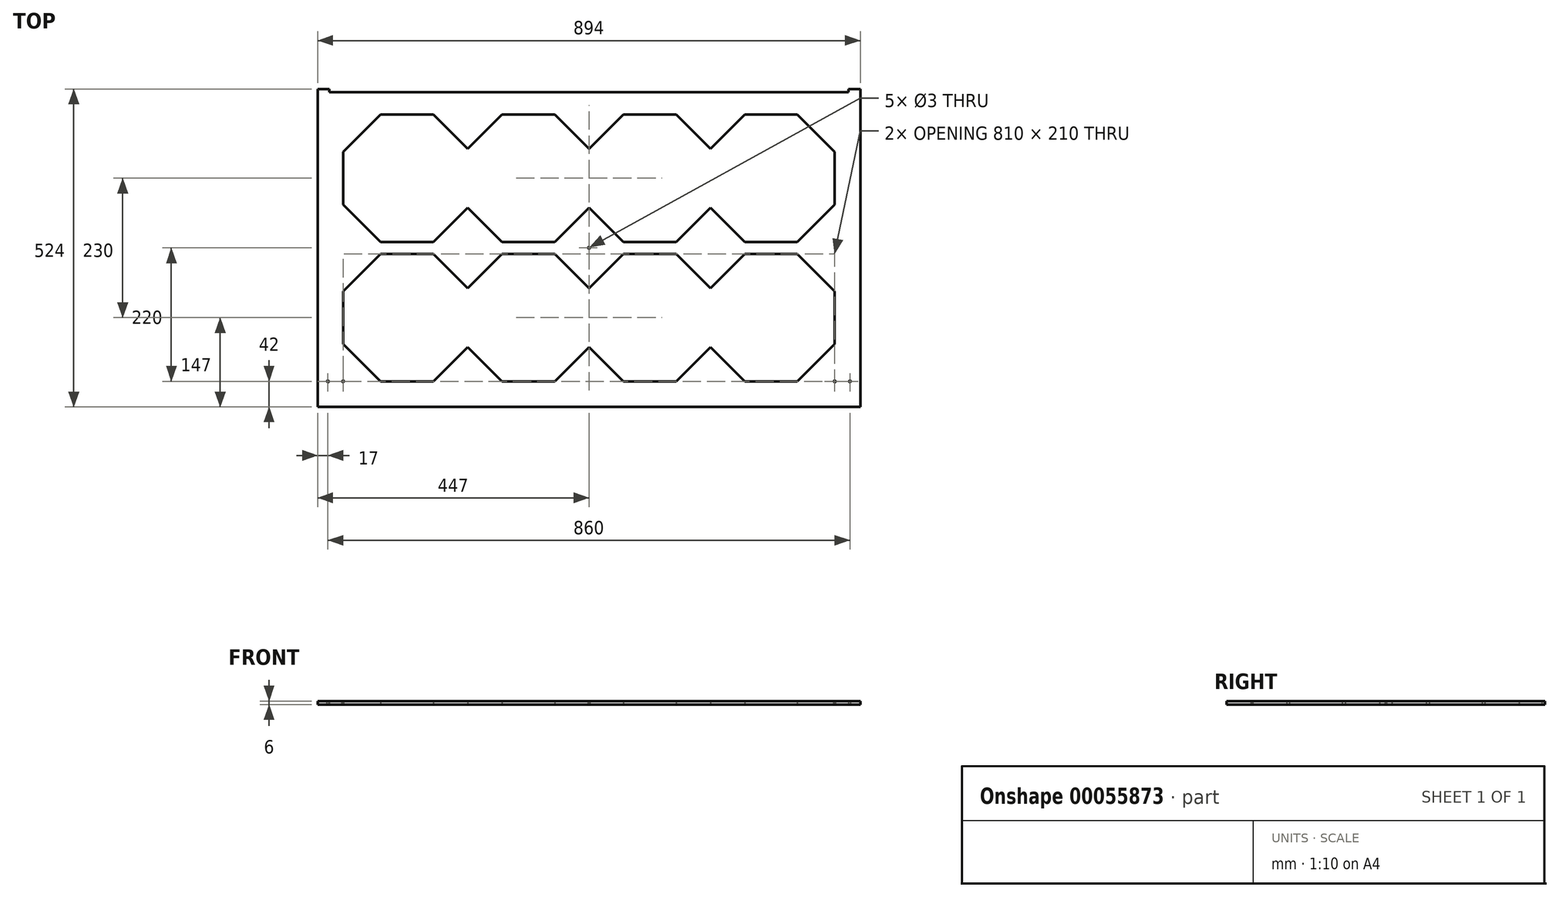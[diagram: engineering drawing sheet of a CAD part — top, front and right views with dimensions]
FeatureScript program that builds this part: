
annotation { "Feature Type Name" : "Feature", "Feature Type Description" : "" }
export const myFeature = defineFeature(function(context is Context, id is Id, definition is map)
    precondition{}
    {
        {
            var Q0;
            Q0=qCreatedBy(makeId("Top.planeOp"),FACE);
            var sketch = newSketch(context, id + "F0", { "sketchPlane" : qUnion([Q0])});
            skCircle(sketch, "E0.cCircle", {"center": v(0, 0) * mm, "radius": 100 * mm, "construction": true});
            skLineSegment(sketch, "E0.0", {"start": v(-41.42, 100) * mm, "end": v(41.42, 100) * mm});
            skLineSegment(sketch, "E0.1", {"start": v(41.42, 100) * mm, "end": v(100, 41.42) * mm});
            skLineSegment(sketch, "E0.2", {"start": v(100, 41.42) * mm, "end": v(100, -41.42) * mm});
            skLineSegment(sketch, "E0.3", {"start": v(100, -41.42) * mm, "end": v(41.42, -100) * mm});
            skLineSegment(sketch, "E0.4", {"start": v(41.42, -100) * mm, "end": v(-41.42, -100) * mm});
            skLineSegment(sketch, "E0.5", {"start": v(-41.42, -100) * mm, "end": v(-100, -41.42) * mm});
            skLineSegment(sketch, "E0.6", {"start": v(-100, -41.42) * mm, "end": v(-100, 41.42) * mm});
            skLineSegment(sketch, "E0.7", {"start": v(-100, 41.42) * mm, "end": v(-41.42, 100) * mm});
            skPoint(sketch, "E0.0.midPoint", {"position": v(0, 100) * mm});
            skCircle(sketch, "E1", {"center": v(-31.79, 31.79) * mm, "radius": 1.3 * mm, "construction": true});
            skCircle(sketch, "E2", {"center": v(31.79, 31.79) * mm, "radius": 1.3 * mm, "construction": true});
            skCircle(sketch, "E3", {"center": v(-31.79, -31.79) * mm, "radius": 1.3 * mm, "construction": true});
            skCircle(sketch, "E4", {"center": v(31.79, -31.79) * mm, "radius": 1.3 * mm, "construction": true});
            skLineSegment(sketch, "E5", {"start": v(0, 0) * mm, "end": v(13.6, 0) * mm, "construction": true});
            skPoint(sketch, "E6", {"position": v(0, -42.85) * mm});
            skLineSegment(sketch, "E7", {"start": v(0, -42.85) * mm, "end": v(66.68, -42.85) * mm, "construction": true});
            skLineSegment(sketch, "E8", {"start": v(0, -42.85) * mm, "end": v(-66.68, -42.85) * mm, "construction": true});
            skCircle(sketch, "E9", {"center": v(-66.68, -42.85) * mm, "radius": 3.81 * mm});
            skCircle(sketch, "E10", {"center": v(66.68, -42.85) * mm, "radius": 3.81 * mm});
            skLineSegment(sketch, "E11", {"start": v(0, 0) * mm, "end": v(0, -42.85) * mm, "construction": true});
            skLineSegment(sketch, "E12.bottom", {"start": v(765, -453) * mm, "end": v(-147, -453) * mm, "construction": true});
            skLineSegment(sketch, "E12.top", {"start": v(765, 147) * mm, "end": v(705, 147) * mm, "construction": true});
            skLineSegment(sketch, "E12.left", {"start": v(765, -453) * mm, "end": v(765, 147) * mm, "construction": true});
            skLineSegment(sketch, "E12.right", {"start": v(-147, -453) * mm, "end": v(-147, 147) * mm, "construction": true});
            skPoint(sketch, "E12.middle", {"position": v(309, -153) * mm});
            skLineSegment(sketch, "E13.0", {"start": v(-43.5, 105) * mm, "end": v(43.5, 105) * mm});
            skLineSegment(sketch, "E13.1", {"start": v(-105, 43.5) * mm, "end": v(-43.5, 105) * mm});
            skLineSegment(sketch, "E13.2", {"start": v(43.5, 105) * mm, "end": v(105, 43.5) * mm});
            skLineSegment(sketch, "E13.3", {"start": v(-105, -43.5) * mm, "end": v(-105, 43.5) * mm});
            skLineSegment(sketch, "E13.4", {"start": v(105, 43.5) * mm, "end": v(105, -43.5) * mm});
            skLineSegment(sketch, "E13.5", {"start": v(105, -43.5) * mm, "end": v(43.5, -105) * mm});
            skLineSegment(sketch, "E13.6", {"start": v(43.5, -105) * mm, "end": v(-43.5, -105) * mm});
            skLineSegment(sketch, "E13.7", {"start": v(-43.5, -105) * mm, "end": v(-105, -43.5) * mm});
            skLineSegment(sketch, "E14.0.1.0", {"start": v(0, -272.85) * mm, "end": v(66.68, -272.85) * mm, "construction": true});
            skLineSegment(sketch, "E14.0.1.1", {"start": v(-43.5, -335) * mm, "end": v(-105, -273.5) * mm});
            skLineSegment(sketch, "E14.0.1.2", {"start": v(-105, -273.5) * mm, "end": v(-105, -186.5) * mm});
            skLineSegment(sketch, "E14.0.1.3", {"start": v(105, -273.5) * mm, "end": v(43.5, -335) * mm});
            skLineSegment(sketch, "E14.0.1.4", {"start": v(-105, -186.5) * mm, "end": v(-43.5, -125) * mm});
            skPoint(sketch, "E14.0.1.5", {"position": v(0, -130) * mm});
            skLineSegment(sketch, "E14.0.1.6", {"start": v(100, -271.42) * mm, "end": v(41.42, -330) * mm, "construction": true});
            skPoint(sketch, "E14.0.1.7", {"position": v(0, -230) * mm});
            skLineSegment(sketch, "E14.0.1.8", {"start": v(-100, -271.42) * mm, "end": v(-100, -188.58) * mm, "construction": true});
            skLineSegment(sketch, "E14.0.1.9", {"start": v(-41.42, -330) * mm, "end": v(-100, -271.42) * mm, "construction": true});
            skLineSegment(sketch, "E14.0.1.10", {"start": v(-100, -188.58) * mm, "end": v(-41.42, -130) * mm, "construction": true});
            skLineSegment(sketch, "E14.0.1.11", {"start": v(100, -188.58) * mm, "end": v(100, -271.42) * mm, "construction": true});
            skLineSegment(sketch, "E14.0.1.12", {"start": v(41.42, -130) * mm, "end": v(100, -188.58) * mm, "construction": true});
            skLineSegment(sketch, "E14.0.1.13", {"start": v(0, -272.85) * mm, "end": v(-66.68, -272.85) * mm, "construction": true});
            skCircle(sketch, "E14.0.1.14", {"center": v(0, -230) * mm, "radius": 100 * mm, "construction": true});
            skLineSegment(sketch, "E14.0.1.15", {"start": v(-41.42, -130) * mm, "end": v(41.42, -130) * mm, "construction": true});
            skLineSegment(sketch, "E14.0.1.16", {"start": v(41.42, -330) * mm, "end": v(-41.42, -330) * mm, "construction": true});
            skLineSegment(sketch, "E14.0.1.17", {"start": v(105, -186.5) * mm, "end": v(105, -273.5) * mm});
            skLineSegment(sketch, "E14.0.1.18", {"start": v(43.5, -125) * mm, "end": v(105, -186.5) * mm});
            skLineSegment(sketch, "E14.0.1.19", {"start": v(-43.5, -125) * mm, "end": v(43.5, -125) * mm});
            skLineSegment(sketch, "E14.0.1.20", {"start": v(43.5, -335) * mm, "end": v(-43.5, -335) * mm});
            skLineSegment(sketch, "E14.0.1.21", {"start": v(0, -230) * mm, "end": v(0, -272.85) * mm, "construction": true});
            skPoint(sketch, "E14.0.1.22", {"position": v(0, -272.85) * mm});
            skLineSegment(sketch, "E14.0.1.23", {"start": v(0, -230) * mm, "end": v(13.6, -230) * mm, "construction": true});
            skPoint(sketch, "E14.0.1.24", {"position": v(0, -230) * mm});
            skCircle(sketch, "E14.0.1.25", {"center": v(66.68, -272.85) * mm, "radius": 3.81 * mm});
            skCircle(sketch, "E14.0.1.26", {"center": v(31.79, -198.21) * mm, "radius": 1.3 * mm, "construction": true});
            skCircle(sketch, "E14.0.1.27", {"center": v(-31.79, -198.21) * mm, "radius": 1.3 * mm, "construction": true});
            skCircle(sketch, "E14.0.1.28", {"center": v(-31.79, -261.79) * mm, "radius": 1.3 * mm, "construction": true});
            skCircle(sketch, "E14.0.1.29", {"center": v(31.79, -261.79) * mm, "radius": 1.3 * mm, "construction": true});
            skCircle(sketch, "E14.0.1.30", {"center": v(-66.68, -272.85) * mm, "radius": 3.81 * mm});
            skLineSegment(sketch, "E14.1.0.0", {"start": v(200, -42.85) * mm, "end": v(266.68, -42.85) * mm, "construction": true});
            skLineSegment(sketch, "E14.1.0.1", {"start": v(156.5, -105) * mm, "end": v(95, -43.5) * mm});
            skLineSegment(sketch, "E14.1.0.2", {"start": v(95, -43.5) * mm, "end": v(95, 43.5) * mm});
            skLineSegment(sketch, "E14.1.0.3", {"start": v(305, -43.5) * mm, "end": v(243.5, -105) * mm});
            skLineSegment(sketch, "E14.1.0.4", {"start": v(95, 43.5) * mm, "end": v(156.5, 105) * mm});
            skPoint(sketch, "E14.1.0.5", {"position": v(200, 100) * mm});
            skLineSegment(sketch, "E14.1.0.6", {"start": v(300, -41.42) * mm, "end": v(241.42, -100) * mm, "construction": true});
            skPoint(sketch, "E14.1.0.7", {"position": v(200, 0) * mm});
            skLineSegment(sketch, "E14.1.0.8", {"start": v(100, -41.42) * mm, "end": v(100, 41.42) * mm, "construction": true});
            skLineSegment(sketch, "E14.1.0.9", {"start": v(158.58, -100) * mm, "end": v(100, -41.42) * mm, "construction": true});
            skLineSegment(sketch, "E14.1.0.10", {"start": v(100, 41.42) * mm, "end": v(158.58, 100) * mm, "construction": true});
            skLineSegment(sketch, "E14.1.0.11", {"start": v(300, 41.42) * mm, "end": v(300, -41.42) * mm, "construction": true});
            skLineSegment(sketch, "E14.1.0.12", {"start": v(241.42, 100) * mm, "end": v(300, 41.42) * mm, "construction": true});
            skLineSegment(sketch, "E14.1.0.13", {"start": v(200, -42.85) * mm, "end": v(133.32, -42.85) * mm, "construction": true});
            skCircle(sketch, "E14.1.0.14", {"center": v(200, 0) * mm, "radius": 100 * mm, "construction": true});
            skLineSegment(sketch, "E14.1.0.15", {"start": v(158.58, 100) * mm, "end": v(241.42, 100) * mm, "construction": true});
            skLineSegment(sketch, "E14.1.0.16", {"start": v(241.42, -100) * mm, "end": v(158.58, -100) * mm, "construction": true});
            skLineSegment(sketch, "E14.1.0.17", {"start": v(305, 43.5) * mm, "end": v(305, -43.5) * mm});
            skLineSegment(sketch, "E14.1.0.18", {"start": v(243.5, 105) * mm, "end": v(305, 43.5) * mm});
            skLineSegment(sketch, "E14.1.0.19", {"start": v(156.5, 105) * mm, "end": v(243.5, 105) * mm});
            skLineSegment(sketch, "E14.1.0.20", {"start": v(243.5, -105) * mm, "end": v(156.5, -105) * mm});
            skLineSegment(sketch, "E14.1.0.21", {"start": v(200, 0) * mm, "end": v(200, -42.85) * mm, "construction": true});
            skPoint(sketch, "E14.1.0.22", {"position": v(200, -42.85) * mm});
            skLineSegment(sketch, "E14.1.0.23", {"start": v(200, 0) * mm, "end": v(213.6, 0) * mm, "construction": true});
            skPoint(sketch, "E14.1.0.24", {"position": v(200, 0) * mm});
            skCircle(sketch, "E14.1.0.25", {"center": v(266.68, -42.85) * mm, "radius": 3.81 * mm});
            skCircle(sketch, "E14.1.0.26", {"center": v(231.79, 31.79) * mm, "radius": 1.3 * mm, "construction": true});
            skCircle(sketch, "E14.1.0.27", {"center": v(168.21, 31.79) * mm, "radius": 1.3 * mm, "construction": true});
            skCircle(sketch, "E14.1.0.28", {"center": v(168.21, -31.79) * mm, "radius": 1.3 * mm, "construction": true});
            skCircle(sketch, "E14.1.0.29", {"center": v(231.79, -31.79) * mm, "radius": 1.3 * mm, "construction": true});
            skCircle(sketch, "E14.1.0.30", {"center": v(133.32, -42.85) * mm, "radius": 3.81 * mm});
            skLineSegment(sketch, "E14.1.1.0", {"start": v(200, -272.85) * mm, "end": v(266.68, -272.85) * mm, "construction": true});
            skLineSegment(sketch, "E14.1.1.1", {"start": v(156.5, -335) * mm, "end": v(95, -273.5) * mm});
            skLineSegment(sketch, "E14.1.1.2", {"start": v(95, -273.5) * mm, "end": v(95, -186.5) * mm});
            skLineSegment(sketch, "E14.1.1.3", {"start": v(305, -273.5) * mm, "end": v(243.5, -335) * mm});
            skLineSegment(sketch, "E14.1.1.4", {"start": v(95, -186.5) * mm, "end": v(156.5, -125) * mm});
            skPoint(sketch, "E14.1.1.5", {"position": v(200, -130) * mm});
            skLineSegment(sketch, "E14.1.1.6", {"start": v(300, -271.42) * mm, "end": v(241.42, -330) * mm, "construction": true});
            skPoint(sketch, "E14.1.1.7", {"position": v(200, -230) * mm});
            skLineSegment(sketch, "E14.1.1.8", {"start": v(100, -271.42) * mm, "end": v(100, -188.58) * mm, "construction": true});
            skLineSegment(sketch, "E14.1.1.9", {"start": v(158.58, -330) * mm, "end": v(100, -271.42) * mm, "construction": true});
            skLineSegment(sketch, "E14.1.1.10", {"start": v(100, -188.58) * mm, "end": v(158.58, -130) * mm, "construction": true});
            skLineSegment(sketch, "E14.1.1.11", {"start": v(300, -188.58) * mm, "end": v(300, -271.42) * mm, "construction": true});
            skLineSegment(sketch, "E14.1.1.12", {"start": v(241.42, -130) * mm, "end": v(300, -188.58) * mm, "construction": true});
            skLineSegment(sketch, "E14.1.1.13", {"start": v(200, -272.85) * mm, "end": v(133.32, -272.85) * mm, "construction": true});
            skCircle(sketch, "E14.1.1.14", {"center": v(200, -230) * mm, "radius": 100 * mm, "construction": true});
            skLineSegment(sketch, "E14.1.1.15", {"start": v(158.58, -130) * mm, "end": v(241.42, -130) * mm, "construction": true});
            skLineSegment(sketch, "E14.1.1.16", {"start": v(241.42, -330) * mm, "end": v(158.58, -330) * mm, "construction": true});
            skLineSegment(sketch, "E14.1.1.17", {"start": v(305, -186.5) * mm, "end": v(305, -273.5) * mm});
            skLineSegment(sketch, "E14.1.1.18", {"start": v(243.5, -125) * mm, "end": v(305, -186.5) * mm});
            skLineSegment(sketch, "E14.1.1.19", {"start": v(156.5, -125) * mm, "end": v(243.5, -125) * mm});
            skLineSegment(sketch, "E14.1.1.20", {"start": v(243.5, -335) * mm, "end": v(156.5, -335) * mm});
            skLineSegment(sketch, "E14.1.1.21", {"start": v(200, -230) * mm, "end": v(200, -272.85) * mm, "construction": true});
            skPoint(sketch, "E14.1.1.22", {"position": v(200, -272.85) * mm});
            skLineSegment(sketch, "E14.1.1.23", {"start": v(200, -230) * mm, "end": v(213.6, -230) * mm, "construction": true});
            skPoint(sketch, "E14.1.1.24", {"position": v(200, -230) * mm});
            skCircle(sketch, "E14.1.1.25", {"center": v(266.68, -272.85) * mm, "radius": 3.81 * mm});
            skCircle(sketch, "E14.1.1.26", {"center": v(231.79, -198.21) * mm, "radius": 1.3 * mm, "construction": true});
            skCircle(sketch, "E14.1.1.27", {"center": v(168.21, -198.21) * mm, "radius": 1.3 * mm, "construction": true});
            skCircle(sketch, "E14.1.1.28", {"center": v(168.21, -261.79) * mm, "radius": 1.3 * mm, "construction": true});
            skCircle(sketch, "E14.1.1.29", {"center": v(231.79, -261.79) * mm, "radius": 1.3 * mm, "construction": true});
            skCircle(sketch, "E14.1.1.30", {"center": v(133.32, -272.85) * mm, "radius": 3.81 * mm});
            skLineSegment(sketch, "E14.2.0.0", {"start": v(400, -42.85) * mm, "end": v(466.68, -42.85) * mm, "construction": true});
            skLineSegment(sketch, "E14.2.0.1", {"start": v(356.5, -105) * mm, "end": v(295, -43.5) * mm});
            skLineSegment(sketch, "E14.2.0.2", {"start": v(295, -43.5) * mm, "end": v(295, 43.5) * mm});
            skLineSegment(sketch, "E14.2.0.3", {"start": v(505, -43.5) * mm, "end": v(443.5, -105) * mm});
            skLineSegment(sketch, "E14.2.0.4", {"start": v(295, 43.5) * mm, "end": v(356.5, 105) * mm});
            skPoint(sketch, "E14.2.0.5", {"position": v(400, 100) * mm});
            skLineSegment(sketch, "E14.2.0.6", {"start": v(500, -41.42) * mm, "end": v(441.42, -100) * mm, "construction": true});
            skPoint(sketch, "E14.2.0.7", {"position": v(400, 0) * mm});
            skLineSegment(sketch, "E14.2.0.8", {"start": v(300, -41.42) * mm, "end": v(300, 41.42) * mm, "construction": true});
            skLineSegment(sketch, "E14.2.0.9", {"start": v(358.58, -100) * mm, "end": v(300, -41.42) * mm, "construction": true});
            skLineSegment(sketch, "E14.2.0.10", {"start": v(300, 41.42) * mm, "end": v(358.58, 100) * mm, "construction": true});
            skLineSegment(sketch, "E14.2.0.11", {"start": v(500, 41.42) * mm, "end": v(500, -41.42) * mm, "construction": true});
            skLineSegment(sketch, "E14.2.0.12", {"start": v(441.42, 100) * mm, "end": v(500, 41.42) * mm, "construction": true});
            skLineSegment(sketch, "E14.2.0.13", {"start": v(400, -42.85) * mm, "end": v(333.32, -42.85) * mm, "construction": true});
            skCircle(sketch, "E14.2.0.14", {"center": v(400, 0) * mm, "radius": 100 * mm, "construction": true});
            skLineSegment(sketch, "E14.2.0.15", {"start": v(358.58, 100) * mm, "end": v(441.42, 100) * mm, "construction": true});
            skLineSegment(sketch, "E14.2.0.16", {"start": v(441.42, -100) * mm, "end": v(358.58, -100) * mm, "construction": true});
            skLineSegment(sketch, "E14.2.0.17", {"start": v(505, 43.5) * mm, "end": v(505, -43.5) * mm});
            skLineSegment(sketch, "E14.2.0.18", {"start": v(443.5, 105) * mm, "end": v(505, 43.5) * mm});
            skLineSegment(sketch, "E14.2.0.19", {"start": v(356.5, 105) * mm, "end": v(443.5, 105) * mm});
            skLineSegment(sketch, "E14.2.0.20", {"start": v(443.5, -105) * mm, "end": v(356.5, -105) * mm});
            skLineSegment(sketch, "E14.2.0.21", {"start": v(400, 0) * mm, "end": v(400, -42.85) * mm, "construction": true});
            skPoint(sketch, "E14.2.0.22", {"position": v(400, -42.85) * mm});
            skLineSegment(sketch, "E14.2.0.23", {"start": v(400, 0) * mm, "end": v(413.6, 0) * mm, "construction": true});
            skPoint(sketch, "E14.2.0.24", {"position": v(400, 0) * mm});
            skCircle(sketch, "E14.2.0.25", {"center": v(466.68, -42.85) * mm, "radius": 3.81 * mm});
            skCircle(sketch, "E14.2.0.26", {"center": v(431.79, 31.79) * mm, "radius": 1.3 * mm, "construction": true});
            skCircle(sketch, "E14.2.0.27", {"center": v(368.21, 31.79) * mm, "radius": 1.3 * mm, "construction": true});
            skCircle(sketch, "E14.2.0.28", {"center": v(368.21, -31.79) * mm, "radius": 1.3 * mm, "construction": true});
            skCircle(sketch, "E14.2.0.29", {"center": v(431.79, -31.79) * mm, "radius": 1.3 * mm, "construction": true});
            skCircle(sketch, "E14.2.0.30", {"center": v(333.32, -42.85) * mm, "radius": 3.81 * mm});
            skLineSegment(sketch, "E14.2.1.0", {"start": v(400, -272.85) * mm, "end": v(466.68, -272.85) * mm, "construction": true});
            skLineSegment(sketch, "E14.2.1.1", {"start": v(356.5, -335) * mm, "end": v(295, -273.5) * mm});
            skLineSegment(sketch, "E14.2.1.2", {"start": v(295, -273.5) * mm, "end": v(295, -186.5) * mm});
            skLineSegment(sketch, "E14.2.1.3", {"start": v(505, -273.5) * mm, "end": v(443.5, -335) * mm});
            skLineSegment(sketch, "E14.2.1.4", {"start": v(295, -186.5) * mm, "end": v(356.5, -125) * mm});
            skPoint(sketch, "E14.2.1.5", {"position": v(400, -130) * mm});
            skLineSegment(sketch, "E14.2.1.6", {"start": v(500, -271.42) * mm, "end": v(441.42, -330) * mm, "construction": true});
            skPoint(sketch, "E14.2.1.7", {"position": v(400, -230) * mm});
            skLineSegment(sketch, "E14.2.1.8", {"start": v(300, -271.42) * mm, "end": v(300, -188.58) * mm, "construction": true});
            skLineSegment(sketch, "E14.2.1.9", {"start": v(358.58, -330) * mm, "end": v(300, -271.42) * mm, "construction": true});
            skLineSegment(sketch, "E14.2.1.10", {"start": v(300, -188.58) * mm, "end": v(358.58, -130) * mm, "construction": true});
            skLineSegment(sketch, "E14.2.1.11", {"start": v(500, -188.58) * mm, "end": v(500, -271.42) * mm, "construction": true});
            skLineSegment(sketch, "E14.2.1.12", {"start": v(441.42, -130) * mm, "end": v(500, -188.58) * mm, "construction": true});
            skLineSegment(sketch, "E14.2.1.13", {"start": v(400, -272.85) * mm, "end": v(333.32, -272.85) * mm, "construction": true});
            skCircle(sketch, "E14.2.1.14", {"center": v(400, -230) * mm, "radius": 100 * mm, "construction": true});
            skLineSegment(sketch, "E14.2.1.15", {"start": v(358.58, -130) * mm, "end": v(441.42, -130) * mm, "construction": true});
            skLineSegment(sketch, "E14.2.1.16", {"start": v(441.42, -330) * mm, "end": v(358.58, -330) * mm, "construction": true});
            skLineSegment(sketch, "E14.2.1.17", {"start": v(505, -186.5) * mm, "end": v(505, -273.5) * mm});
            skLineSegment(sketch, "E14.2.1.18", {"start": v(443.5, -125) * mm, "end": v(505, -186.5) * mm});
            skLineSegment(sketch, "E14.2.1.19", {"start": v(356.5, -125) * mm, "end": v(443.5, -125) * mm});
            skLineSegment(sketch, "E14.2.1.20", {"start": v(443.5, -335) * mm, "end": v(356.5, -335) * mm});
            skLineSegment(sketch, "E14.2.1.21", {"start": v(400, -230) * mm, "end": v(400, -272.85) * mm, "construction": true});
            skPoint(sketch, "E14.2.1.22", {"position": v(400, -272.85) * mm});
            skLineSegment(sketch, "E14.2.1.23", {"start": v(400, -230) * mm, "end": v(413.6, -230) * mm, "construction": true});
            skPoint(sketch, "E14.2.1.24", {"position": v(400, -230) * mm});
            skCircle(sketch, "E14.2.1.25", {"center": v(466.68, -272.85) * mm, "radius": 3.81 * mm});
            skCircle(sketch, "E14.2.1.26", {"center": v(431.79, -198.21) * mm, "radius": 1.3 * mm, "construction": true});
            skCircle(sketch, "E14.2.1.27", {"center": v(368.21, -198.21) * mm, "radius": 1.3 * mm, "construction": true});
            skCircle(sketch, "E14.2.1.28", {"center": v(368.21, -261.79) * mm, "radius": 1.3 * mm, "construction": true});
            skCircle(sketch, "E14.2.1.29", {"center": v(431.79, -261.79) * mm, "radius": 1.3 * mm, "construction": true});
            skCircle(sketch, "E14.2.1.30", {"center": v(333.32, -272.85) * mm, "radius": 3.81 * mm});
            skLineSegment(sketch, "E14.3.0.0", {"start": v(600, -42.85) * mm, "end": v(666.68, -42.85) * mm, "construction": true});
            skLineSegment(sketch, "E14.3.0.1", {"start": v(556.5, -105) * mm, "end": v(495, -43.5) * mm});
            skLineSegment(sketch, "E14.3.0.2", {"start": v(495, -43.5) * mm, "end": v(495, 43.5) * mm});
            skLineSegment(sketch, "E14.3.0.3", {"start": v(705, -43.5) * mm, "end": v(643.5, -105) * mm});
            skLineSegment(sketch, "E14.3.0.4", {"start": v(495, 43.5) * mm, "end": v(556.5, 105) * mm});
            skPoint(sketch, "E14.3.0.5", {"position": v(600, 100) * mm});
            skLineSegment(sketch, "E14.3.0.6", {"start": v(700, -41.42) * mm, "end": v(641.42, -100) * mm, "construction": true});
            skPoint(sketch, "E14.3.0.7", {"position": v(600, 0) * mm});
            skLineSegment(sketch, "E14.3.0.8", {"start": v(500, -41.42) * mm, "end": v(500, 41.42) * mm, "construction": true});
            skLineSegment(sketch, "E14.3.0.9", {"start": v(558.58, -100) * mm, "end": v(500, -41.42) * mm, "construction": true});
            skLineSegment(sketch, "E14.3.0.10", {"start": v(500, 41.42) * mm, "end": v(558.58, 100) * mm, "construction": true});
            skLineSegment(sketch, "E14.3.0.11", {"start": v(700, 41.42) * mm, "end": v(700, -41.42) * mm, "construction": true});
            skLineSegment(sketch, "E14.3.0.12", {"start": v(641.42, 100) * mm, "end": v(700, 41.42) * mm, "construction": true});
            skLineSegment(sketch, "E14.3.0.13", {"start": v(600, -42.85) * mm, "end": v(533.33, -42.85) * mm, "construction": true});
            skCircle(sketch, "E14.3.0.14", {"center": v(600, 0) * mm, "radius": 100 * mm, "construction": true});
            skLineSegment(sketch, "E14.3.0.15", {"start": v(558.58, 100) * mm, "end": v(641.42, 100) * mm, "construction": true});
            skLineSegment(sketch, "E14.3.0.16", {"start": v(641.42, -100) * mm, "end": v(558.58, -100) * mm, "construction": true});
            skLineSegment(sketch, "E14.3.0.17", {"start": v(705, 43.5) * mm, "end": v(705, -43.5) * mm});
            skLineSegment(sketch, "E14.3.0.18", {"start": v(643.5, 105) * mm, "end": v(705, 43.5) * mm});
            skLineSegment(sketch, "E14.3.0.19", {"start": v(556.5, 105) * mm, "end": v(643.5, 105) * mm});
            skLineSegment(sketch, "E14.3.0.20", {"start": v(643.5, -105) * mm, "end": v(556.5, -105) * mm});
            skLineSegment(sketch, "E14.3.0.21", {"start": v(600, 0) * mm, "end": v(600, -42.85) * mm, "construction": true});
            skPoint(sketch, "E14.3.0.22", {"position": v(600, -42.85) * mm});
            skLineSegment(sketch, "E14.3.0.23", {"start": v(600, 0) * mm, "end": v(613.6, 0) * mm, "construction": true});
            skPoint(sketch, "E14.3.0.24", {"position": v(600, 0) * mm});
            skCircle(sketch, "E14.3.0.25", {"center": v(666.68, -42.85) * mm, "radius": 3.81 * mm});
            skCircle(sketch, "E14.3.0.26", {"center": v(631.79, 31.79) * mm, "radius": 1.3 * mm, "construction": true});
            skCircle(sketch, "E14.3.0.27", {"center": v(568.21, 31.79) * mm, "radius": 1.3 * mm, "construction": true});
            skCircle(sketch, "E14.3.0.28", {"center": v(568.21, -31.79) * mm, "radius": 1.3 * mm, "construction": true});
            skCircle(sketch, "E14.3.0.29", {"center": v(631.79, -31.79) * mm, "radius": 1.3 * mm, "construction": true});
            skCircle(sketch, "E14.3.0.30", {"center": v(533.33, -42.85) * mm, "radius": 3.81 * mm});
            skLineSegment(sketch, "E14.3.1.0", {"start": v(600, -272.85) * mm, "end": v(666.68, -272.85) * mm, "construction": true});
            skLineSegment(sketch, "E14.3.1.1", {"start": v(556.5, -335) * mm, "end": v(495, -273.5) * mm});
            skLineSegment(sketch, "E14.3.1.2", {"start": v(495, -273.5) * mm, "end": v(495, -186.5) * mm});
            skLineSegment(sketch, "E14.3.1.3", {"start": v(705, -273.5) * mm, "end": v(643.5, -335) * mm});
            skLineSegment(sketch, "E14.3.1.4", {"start": v(495, -186.5) * mm, "end": v(556.5, -125) * mm});
            skPoint(sketch, "E14.3.1.5", {"position": v(600, -130) * mm});
            skLineSegment(sketch, "E14.3.1.6", {"start": v(700, -271.42) * mm, "end": v(641.42, -330) * mm, "construction": true});
            skPoint(sketch, "E14.3.1.7", {"position": v(600, -230) * mm});
            skLineSegment(sketch, "E14.3.1.8", {"start": v(500, -271.42) * mm, "end": v(500, -188.58) * mm, "construction": true});
            skLineSegment(sketch, "E14.3.1.9", {"start": v(558.58, -330) * mm, "end": v(500, -271.42) * mm, "construction": true});
            skLineSegment(sketch, "E14.3.1.10", {"start": v(500, -188.58) * mm, "end": v(558.58, -130) * mm, "construction": true});
            skLineSegment(sketch, "E14.3.1.11", {"start": v(700, -188.58) * mm, "end": v(700, -271.42) * mm, "construction": true});
            skLineSegment(sketch, "E14.3.1.12", {"start": v(641.42, -130) * mm, "end": v(700, -188.58) * mm, "construction": true});
            skLineSegment(sketch, "E14.3.1.13", {"start": v(600, -272.85) * mm, "end": v(533.33, -272.85) * mm, "construction": true});
            skCircle(sketch, "E14.3.1.14", {"center": v(600, -230) * mm, "radius": 100 * mm, "construction": true});
            skLineSegment(sketch, "E14.3.1.15", {"start": v(558.58, -130) * mm, "end": v(641.42, -130) * mm, "construction": true});
            skLineSegment(sketch, "E14.3.1.16", {"start": v(641.42, -330) * mm, "end": v(558.58, -330) * mm, "construction": true});
            skLineSegment(sketch, "E14.3.1.17", {"start": v(705, -186.5) * mm, "end": v(705, -273.5) * mm});
            skLineSegment(sketch, "E14.3.1.18", {"start": v(643.5, -125) * mm, "end": v(705, -186.5) * mm});
            skLineSegment(sketch, "E14.3.1.19", {"start": v(556.5, -125) * mm, "end": v(643.5, -125) * mm});
            skLineSegment(sketch, "E14.3.1.20", {"start": v(643.5, -335) * mm, "end": v(556.5, -335) * mm});
            skLineSegment(sketch, "E14.3.1.21", {"start": v(600, -230) * mm, "end": v(600, -272.85) * mm, "construction": true});
            skPoint(sketch, "E14.3.1.22", {"position": v(600, -272.85) * mm});
            skLineSegment(sketch, "E14.3.1.23", {"start": v(600, -230) * mm, "end": v(613.6, -230) * mm, "construction": true});
            skPoint(sketch, "E14.3.1.24", {"position": v(600, -230) * mm});
            skCircle(sketch, "E14.3.1.25", {"center": v(666.68, -272.85) * mm, "radius": 3.81 * mm});
            skCircle(sketch, "E14.3.1.26", {"center": v(631.79, -198.21) * mm, "radius": 1.3 * mm, "construction": true});
            skCircle(sketch, "E14.3.1.27", {"center": v(568.21, -198.21) * mm, "radius": 1.3 * mm, "construction": true});
            skCircle(sketch, "E14.3.1.28", {"center": v(568.21, -261.79) * mm, "radius": 1.3 * mm, "construction": true});
            skCircle(sketch, "E14.3.1.29", {"center": v(631.79, -261.79) * mm, "radius": 1.3 * mm, "construction": true});
            skCircle(sketch, "E14.3.1.30", {"center": v(533.33, -272.85) * mm, "radius": 3.81 * mm});
            skLineSegment(sketch, "E14.direction1", {"start": v(-43.5, -105) * mm, "end": v(156.5, -105) * mm, "construction": true});
            skLineSegment(sketch, "E14.direction2", {"start": v(-43.5, -105) * mm, "end": v(-43.5, -335) * mm, "construction": true});
            skLineSegment(sketch, "E15.bottom", {"start": v(-147, 147) * mm, "end": v(-105, 147) * mm});
            skLineSegment(sketch, "E15.top", {"start": v(-147, -377) * mm, "end": v(747, -377) * mm});
            skLineSegment(sketch, "E15.left", {"start": v(-147, 147) * mm, "end": v(-147, -377) * mm});
            skLineSegment(sketch, "E15.right", {"start": v(747, 147) * mm, "end": v(747, -377) * mm});
            skLineSegment(sketch, "E16", {"start": v(300, 147) * mm, "end": v(300, -377) * mm, "construction": true});
            skLineSegment(sketch, "E17", {"start": v(-147, -115) * mm, "end": v(747, -115) * mm, "construction": true});
            skCircle(sketch, "E18", {"center": v(300, -115) * mm, "radius": 1.5 * mm});
            skLineSegment(sketch, "E19", {"start": v(-105, 142) * mm, "end": v(705, 142) * mm});
            skLineSegment(sketch, "E20", {"start": v(-105, 43.5) * mm, "end": v(-105, 142) * mm, "construction": true});
            skLineSegment(sketch, "E21.trimOffspring", {"start": v(-105, 147) * mm, "end": v(-147, 147) * mm, "construction": true});
            skLineSegment(sketch, "E22.trimOffspring", {"start": v(705, 147) * mm, "end": v(747, 147) * mm});
            skPoint(sketch, "E23", {"position": v(300, 142) * mm});
            skLineSegment(sketch, "E24", {"start": v(-127.5, 142) * mm, "end": v(727.5, 142) * mm});
            skLineSegment(sketch, "E25", {"start": v(-127.5, 142) * mm, "end": v(-127.5, 147) * mm});
            skLineSegment(sketch, "E26", {"start": v(727.5, 142) * mm, "end": v(727.5, 147) * mm});
            skSolve(sketch);
        }
        {
            var Q0;
            Q0=makeQuery(id+"F0.imprint","IMPRINT",FACE,{"disambiguationData":[TD([[makeQuery(id+"F0.imprint","IMPRINT",EDGE,{"derivedFrom":sQuery(id+"F0.wireOp",EDGE,"E13.0")}),1.0]])]});
            extrude(context, id + "F1", {"entities" : qUnion([Q0]), "depth" : 6 * mm});
        }
        {
            var Q0;
            Q0=makeQuery(id+"F1.opExtrude","CAP_FACE",FACE,{"disambiguationData":[OSD([sQuery(id+"F0.wireOp",EDGE,"E13.0"),sQuery(id+"F0.wireOp",EDGE,"E13.1"),sQuery(id+"F0.wireOp",EDGE,"E13.2"),sQuery(id+"F0.wireOp",EDGE,"E13.3"),sQuery(id+"F0.wireOp",EDGE,"E13.5"),sQuery(id+"F0.wireOp",EDGE,"E13.6"),sQuery(id+"F0.wireOp",EDGE,"E13.7"),sQuery(id+"F0.wireOp",EDGE,"E14.0.1.1"),sQuery(id+"F0.wireOp",EDGE,"E14.0.1.2"),sQuery(id+"F0.wireOp",EDGE,"E14.0.1.3"),sQuery(id+"F0.wireOp",EDGE,"E14.0.1.4"),sQuery(id+"F0.wireOp",EDGE,"E14.0.1.18"),sQuery(id+"F0.wireOp",EDGE,"E14.0.1.19"),sQuery(id+"F0.wireOp",EDGE,"E14.0.1.20"),sQuery(id+"F0.wireOp",EDGE,"E14.1.0.1"),sQuery(id+"F0.wireOp",EDGE,"E14.1.0.3"),sQuery(id+"F0.wireOp",EDGE,"E14.1.0.4"),sQuery(id+"F0.wireOp",EDGE,"E14.1.0.18"),sQuery(id+"F0.wireOp",EDGE,"E14.1.0.19"),sQuery(id+"F0.wireOp",EDGE,"E14.1.0.20"),sQuery(id+"F0.wireOp",EDGE,"E14.1.1.1"),sQuery(id+"F0.wireOp",EDGE,"E14.1.1.3"),sQuery(id+"F0.wireOp",EDGE,"E14.1.1.4"),sQuery(id+"F0.wireOp",EDGE,"E14.1.1.18"),sQuery(id+"F0.wireOp",EDGE,"E14.1.1.19"),sQuery(id+"F0.wireOp",EDGE,"E14.1.1.20"),sQuery(id+"F0.wireOp",EDGE,"E14.2.0.1"),sQuery(id+"F0.wireOp",EDGE,"E14.2.0.3"),sQuery(id+"F0.wireOp",EDGE,"E14.2.0.4"),sQuery(id+"F0.wireOp",EDGE,"E14.2.0.18"),sQuery(id+"F0.wireOp",EDGE,"E14.2.0.19"),sQuery(id+"F0.wireOp",EDGE,"E14.2.0.20"),sQuery(id+"F0.wireOp",EDGE,"E14.2.1.1"),sQuery(id+"F0.wireOp",EDGE,"E14.2.1.3"),sQuery(id+"F0.wireOp",EDGE,"E14.2.1.4"),sQuery(id+"F0.wireOp",EDGE,"E14.2.1.18"),sQuery(id+"F0.wireOp",EDGE,"E14.2.1.19"),sQuery(id+"F0.wireOp",EDGE,"E14.2.1.20"),sQuery(id+"F0.wireOp",EDGE,"E14.3.0.1"),sQuery(id+"F0.wireOp",EDGE,"E14.3.0.3"),sQuery(id+"F0.wireOp",EDGE,"E14.3.0.4"),sQuery(id+"F0.wireOp",EDGE,"E14.3.0.17"),sQuery(id+"F0.wireOp",EDGE,"E14.3.0.18"),sQuery(id+"F0.wireOp",EDGE,"E14.3.0.19"),sQuery(id+"F0.wireOp",EDGE,"E14.3.0.20"),sQuery(id+"F0.wireOp",EDGE,"E14.3.1.1"),sQuery(id+"F0.wireOp",EDGE,"E14.3.1.3"),sQuery(id+"F0.wireOp",EDGE,"E14.3.1.4"),sQuery(id+"F0.wireOp",EDGE,"E14.3.1.17"),sQuery(id+"F0.wireOp",EDGE,"E14.3.1.18"),sQuery(id+"F0.wireOp",EDGE,"E14.3.1.19"),sQuery(id+"F0.wireOp",EDGE,"E14.3.1.20"),sQuery(id+"F0.wireOp",EDGE,"E15.bottom"),sQuery(id+"F0.wireOp",EDGE,"E15.top"),sQuery(id+"F0.wireOp",EDGE,"E15.left"),sQuery(id+"F0.wireOp",EDGE,"E15.right"),sQuery(id+"F0.wireOp",EDGE,"E18"),sQuery(id+"F0.wireOp",EDGE,"E22.trimOffspring"),sQuery(id+"F0.wireOp",EDGE,"E24"),sQuery(id+"F0.wireOp",EDGE,"E25"),sQuery(id+"F0.wireOp",EDGE,"E26")])],"isStart":false});
            var sketch = newSketch(context, id + "F2", { "sketchPlane" : qUnion([Q0])});
            skLineSegment(sketch, "E27.0", {"start": v(-105, -273.5) * mm, "end": v(-105, -186.5) * mm});
            skLineSegment(sketch, "E28.0", {"start": v(43.5, -335) * mm, "end": v(-43.5, -335) * mm});
            skLineSegment(sketch, "E29", {"start": v(-105, -273.5) * mm, "end": v(-105, -377) * mm, "construction": true});
            skLineSegment(sketch, "E30", {"start": v(-43.5, -335) * mm, "end": v(-147, -335) * mm, "construction": true});
            skCircle(sketch, "E31", {"center": v(-105, -335) * mm, "radius": 1.5 * mm});
            skCircle(sketch, "E32", {"center": v(-130, -335) * mm, "radius": 1.5 * mm});
            skLineSegment(sketch, "E33", {"start": v(300, -377) * mm, "end": v(300, 142) * mm, "construction": true});
            skCircle(sketch, "E34.MirrorC", {"center": v(705, -335) * mm, "radius": 1.5 * mm});
            skCircle(sketch, "E35.MirrorC", {"center": v(730, -335) * mm, "radius": 1.5 * mm});
            skSolve(sketch);
        }
        {
            var Q0;
            Q0 = qSketchRegion(id + "F2", true);
            extrude(context, id + "F3", {"entities" : qUnion([Q0]), "operationType" : NewBodyOperationType.REMOVE, "oppositeDirection" : true, "depth" : 25 * mm});
        }
    });
